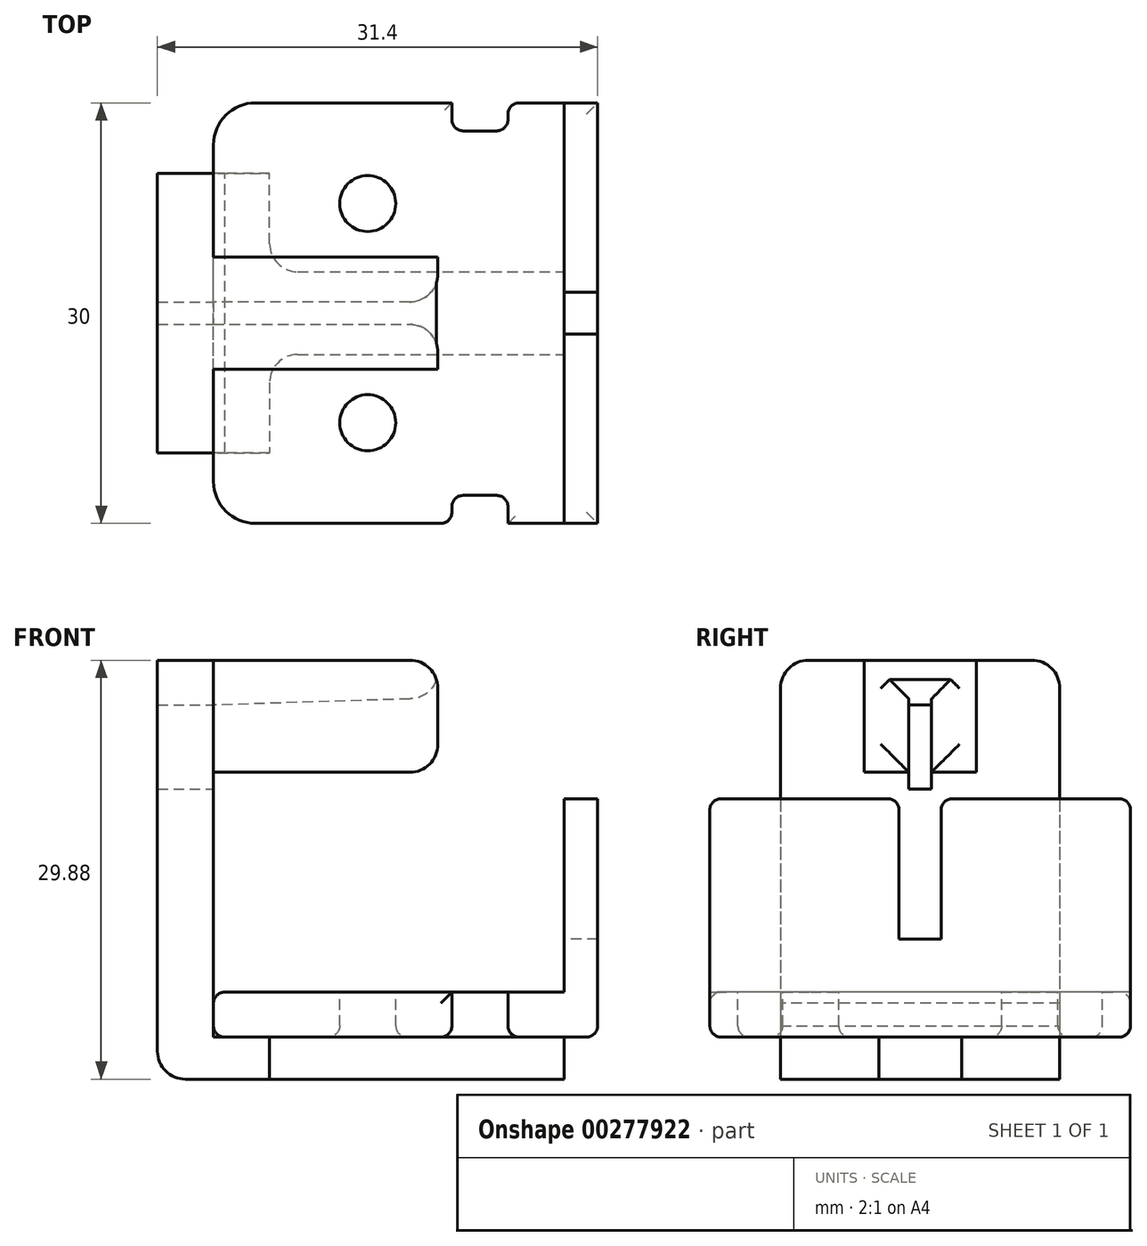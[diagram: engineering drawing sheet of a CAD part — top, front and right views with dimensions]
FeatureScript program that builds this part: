
annotation { "Feature Type Name" : "Feature", "Feature Type Description" : "" }
export const myFeature = defineFeature(function(context is Context, id is Id, definition is map)
    precondition{}
    {
        {
            var Q0;
            Q0=qCreatedBy(makeId("Right.planeOp"),FACE);
            var sketch = newSketch(context, id + "F0", { "sketchPlane" : qUnion([Q0])});
            skPoint(sketch, "E0.middle", {"position": v(0, 9.52) * mm});
            skLineSegment(sketch, "E1.bottom", {"start": v(-15, -0.58) * mm, "end": v(15, -0.58) * mm});
            skLineSegment(sketch, "E2.top", {"start": v(1.5, 6.42) * mm, "end": v(-1.5, 6.42) * mm});
            skLineSegment(sketch, "E2.left", {"start": v(1.5, 14.42) * mm, "end": v(1.5, 6.42) * mm});
            skLineSegment(sketch, "E2.right", {"start": v(-1.5, 14.42) * mm, "end": v(-1.5, 6.42) * mm});
            skPoint(sketch, "E2.middle", {"position": v(0, 10.42) * mm});
            skLineSegment(sketch, "E3", {"start": v(-15, 16.42) * mm, "end": v(-1.5, 16.42) * mm});
            skLineSegment(sketch, "E4", {"start": v(-1.5, 16.42) * mm, "end": v(-1.5, 14.42) * mm});
            skLineSegment(sketch, "E5", {"start": v(1.5, 14.42) * mm, "end": v(1.5, 16.42) * mm});
            skLineSegment(sketch, "E6", {"start": v(1.5, 16.42) * mm, "end": v(15, 16.42) * mm});
            skLineSegment(sketch, "E7", {"start": v(15, 16.42) * mm, "end": v(15, -0.58) * mm});
            skLineSegment(sketch, "E8", {"start": v(-15, -0.58) * mm, "end": v(-15, 16.42) * mm});
            skSolve(sketch);
        }
        {
            var Q0;
            Q0 = qSketchRegion(id + "F0", true);
            extrude(context, id + "F1", {"entities" : qUnion([Q0]), "depth" : 2.4 * mm});
        }
        {
            var Q0;
            Q0=makeQuery(id+"F1.opExtrude","CAP_FACE",FACE,{"disambiguationData":[OSD([sQuery(id+"F0.wireOp",EDGE,"E0.left"),sQuery(id+"F0.wireOp",EDGE,"E0.right"),sQuery(id+"F0.wireOp",EDGE,"E1.bottom"),sQuery(id+"F0.wireOp",EDGE,"E1.left"),sQuery(id+"F0.wireOp",EDGE,"E1.right"),sQuery(id+"F0.wireOp",EDGE,"E2.top"),sQuery(id+"F0.wireOp",EDGE,"E2.left"),sQuery(id+"F0.wireOp",EDGE,"E2.right"),sQuery(id+"F0.wireOp",EDGE,"E3"),sQuery(id+"F0.wireOp",EDGE,"E4"),sQuery(id+"F0.wireOp",EDGE,"E5"),sQuery(id+"F0.wireOp",EDGE,"E6")])],"isStart":true});
            var sketch = newSketch(context, id + "F2", { "sketchPlane" : qUnion([Q0])});
            skLineSegment(sketch, "E9.bottom", {"start": v(-15, -0.58) * mm, "end": v(15, -0.58) * mm});
            skLineSegment(sketch, "E9.top", {"start": v(-15, 2.62) * mm, "end": v(15, 2.62) * mm});
            skLineSegment(sketch, "E9.left", {"start": v(-15, -0.58) * mm, "end": v(-15, 2.62) * mm});
            skLineSegment(sketch, "E9.right", {"start": v(15, -0.58) * mm, "end": v(15, 2.62) * mm});
            skSolve(sketch);
        }
        {
            var Q0;
            Q0 = qSketchRegion(id + "F2", true);
            extrude(context, id + "F3", {"entities" : qUnion([Q0]), "operationType" : NewBodyOperationType.ADD, "depth" : 25 * mm});
        }
        {
            var Q0;
            Q0=makeQuery(id+"F3.opExtrude","SWEPT_FACE",FACE,{"disambiguationData":[OSD([sQuery(id+"F2.wireOp",EDGE,"E9.top")])]});
            var sketch = newSketch(context, id + "F4", { "sketchPlane" : qUnion([Q0])});
            skCircle(sketch, "E10", {"center": v(-14, -7.82) * mm, "radius": 2 * mm});
            skCircle(sketch, "E11.MirrorC", {"center": v(-14, 7.82) * mm, "radius": 2 * mm});
            skCircle(sketch, "E12", {"center": v(-14, 7.82) * mm, "radius": 6 * mm, "construction": true});
            skLineSegment(sketch, "E13", {"start": v(10.5, 1.5) * mm, "end": v(-34.24, 1.5) * mm, "construction": true});
            skLineSegment(sketch, "E14", {"start": v(-34.91, -1.5) * mm, "end": v(11.26, -1.5) * mm, "construction": true});
            skCircle(sketch, "E15.MirrorC", {"center": v(-14, -7.82) * mm, "radius": 6 * mm, "construction": true});
            skSolve(sketch);
        }
        {
            var Q0;
            Q0 = qSketchRegion(id + "F4", true);
            var Q1;
            Q1=makeQuery(id+"F3.boolean.opBoolean","MERGE",FACE,{"derivedFrom":[makeQuery(id+"F1.opExtrude","SWEPT_FACE",FACE,{"disambiguationData":[OSD([sQuery(id+"F0.wireOp",EDGE,"E1.bottom")])]}),makeQuery(id+"F3.opExtrude","SWEPT_FACE",FACE,{"disambiguationData":[OSD([sQuery(id+"F2.wireOp",EDGE,"1xGYJ25z-1f1L-zVY3-qiX9-Y2JeaQydqzHR.bottom")])]})]});
            extrude(context, id + "F5", {"entities" : qUnion([Q0]), "operationType" : NewBodyOperationType.REMOVE, "endBound" : BoundingType.UP_TO_SURFACE, "oppositeDirection" : true, "endBoundEntityFace" : qUnion([Q1]), "depth" : 25 * mm});
        }
        {
            var Q0;
            Q0=makeQuery(id+"F4.imprint","IMPRINT",FACE,{"disambiguationData":[TD([[makeQuery(id+"F4.imprint","IMPRINT",EDGE,{"derivedFrom":sQuery(id+"F4.wireOp",EDGE,"E10")}),-1.0]])]});
            var sketch = newSketch(context, id + "F6", { "sketchPlane" : qUnion([Q0])});
            skLineSegment(sketch, "E16.bottom", {"start": v(-8, 15) * mm, "end": v(-4, 15) * mm});
            skLineSegment(sketch, "E16.top", {"start": v(-8, 13) * mm, "end": v(-4, 13) * mm});
            skLineSegment(sketch, "E16.left", {"start": v(-8, 15) * mm, "end": v(-8, 13) * mm});
            skLineSegment(sketch, "E16.right", {"start": v(-4, 15) * mm, "end": v(-4, 13) * mm});
            skLineSegment(sketch, "E17.MirrorCS", {"start": v(-8, -13) * mm, "end": v(-4, -13) * mm});
            skLineSegment(sketch, "E18.MirrorCS", {"start": v(-4, -15) * mm, "end": v(-4, -13) * mm});
            skLineSegment(sketch, "E19.MirrorCS", {"start": v(-8, -15) * mm, "end": v(-4, -15) * mm});
            skLineSegment(sketch, "E20.MirrorCS", {"start": v(-8, -15) * mm, "end": v(-8, -13) * mm});
            skSolve(sketch);
        }
        {
            var Q0;
            Q0 = qSketchRegion(id + "F6", true);
            var Q1;
            Q1=makeQuery(id+"F3.boolean.opBoolean","MERGE",FACE,{"derivedFrom":[makeQuery(id+"F1.opExtrude","SWEPT_FACE",FACE,{"disambiguationData":[OSD([sQuery(id+"F0.wireOp",EDGE,"E1.bottom")])]}),makeQuery(id+"F3.opExtrude","SWEPT_FACE",FACE,{"disambiguationData":[OSD([sQuery(id+"F2.wireOp",EDGE,"E9.bottom")])]})]});
            extrude(context, id + "F7", {"entities" : qUnion([Q0]), "operationType" : NewBodyOperationType.REMOVE, "endBound" : BoundingType.UP_TO_SURFACE, "oppositeDirection" : true, "endBoundEntityFace" : qUnion([Q1]), "depth" : 25 * mm});
        }
        {
            var Q0;
            Q0=makeQuery(id+"F3.boolean.opBoolean","MERGE",FACE,{"derivedFrom":[makeQuery(id+"F1.opExtrude","SWEPT_FACE",FACE,{"disambiguationData":[OSD([sQuery(id+"F0.wireOp",EDGE,"E1.bottom")])]}),makeQuery(id+"F3.opExtrude","SWEPT_FACE",FACE,{"disambiguationData":[OSD([sQuery(id+"F2.wireOp",EDGE,"1xGYJ25z-1f1L-zVY3-qiX9-Y2JeaQydqzHR.bottom")])]})]});
            var Q1;
            Q1=makeQuery(id+"F1.opExtrude","SWEPT_EDGE",EDGE,{"disambiguationData":[OSD([sQuery(id+"F0.wireOp",EDGE,"E0.left"),sQuery(id+"F0.wireOp",EDGE,"E6")])]});
            var Q2;
            Q2=makeQuery(id+"F1.opExtrude","SWEPT_EDGE",EDGE,{"disambiguationData":[OSD([sQuery(id+"F0.wireOp",EDGE,"E5"),sQuery(id+"F0.wireOp",EDGE,"E6")])]});
            var Q3;
            Q3=makeQuery(id+"F1.opExtrude","SWEPT_EDGE",EDGE,{"disambiguationData":[OSD([sQuery(id+"F0.wireOp",EDGE,"E3"),sQuery(id+"F0.wireOp",EDGE,"E4")])]});
            var Q4;
            Q4=makeQuery(id+"F1.opExtrude","SWEPT_EDGE",EDGE,{"disambiguationData":[OSD([sQuery(id+"F0.wireOp",EDGE,"E0.right"),sQuery(id+"F0.wireOp",EDGE,"E3")])]});
            var Q5;
            Q5=makeQuery(id+"F7.boolean.opBoolean","COPY",EDGE,{"derivedFrom":makeQuery(id+"F7.opExtrude","SWEPT_EDGE",EDGE,{"disambiguationData":[OSD([sQuery(id+"F0.wireOp",EDGE,"E7"),sQuery(id+"F2.wireOp",EDGE,"E9.top"),sQuery(id+"F2.wireOp",EDGE,"E9.left"),sQuery(id+"F6.wireOp",EDGE,"E16.bottom"),sQuery(id+"F6.wireOp",EDGE,"E16.left")])]})});
            var Q6;
            Q6=makeQuery(id+"F7.boolean.opBoolean","COPY",EDGE,{"derivedFrom":makeQuery(id+"F7.opExtrude","SWEPT_EDGE",EDGE,{"disambiguationData":[OSD([sQuery(id+"F0.wireOp",EDGE,"E7"),sQuery(id+"F2.wireOp",EDGE,"E9.top"),sQuery(id+"F2.wireOp",EDGE,"E9.left"),sQuery(id+"F6.wireOp",EDGE,"E16.bottom"),sQuery(id+"F6.wireOp",EDGE,"E16.right")])]})});
            var Q7;
            Q7=makeQuery(id+"F7.boolean.opBoolean","COPY",EDGE,{"derivedFrom":makeQuery(id+"F7.opExtrude","SWEPT_EDGE",EDGE,{"disambiguationData":[OSD([sQuery(id+"F0.wireOp",EDGE,"E8"),sQuery(id+"F2.wireOp",EDGE,"E9.top"),sQuery(id+"F2.wireOp",EDGE,"E9.right"),sQuery(id+"F6.wireOp",EDGE,"E18.MirrorCS"),sQuery(id+"F6.wireOp",EDGE,"E19.MirrorCS")])]})});
            var Q8;
            Q8=makeQuery(id+"F7.boolean.opBoolean","COPY",EDGE,{"derivedFrom":makeQuery(id+"F7.opExtrude","SWEPT_EDGE",EDGE,{"disambiguationData":[OSD([sQuery(id+"F0.wireOp",EDGE,"E8"),sQuery(id+"F2.wireOp",EDGE,"E9.top"),sQuery(id+"F2.wireOp",EDGE,"E9.right"),sQuery(id+"F6.wireOp",EDGE,"E19.MirrorCS"),sQuery(id+"F6.wireOp",EDGE,"E20.MirrorCS")])]})});
            var Q9;
            Q9=makeQuery(id+"F7.boolean.opBoolean","COPY",EDGE,{"derivedFrom":makeQuery(id+"F7.opExtrude","SWEPT_EDGE",EDGE,{"disambiguationData":[OSD([sQuery(id+"F6.wireOp",EDGE,"E17.MirrorCS"),sQuery(id+"F6.wireOp",EDGE,"E18.MirrorCS")])]})});
            var Q10;
            Q10=makeQuery(id+"F7.boolean.opBoolean","COPY",EDGE,{"derivedFrom":makeQuery(id+"F7.opExtrude","SWEPT_EDGE",EDGE,{"disambiguationData":[OSD([sQuery(id+"F6.wireOp",EDGE,"E17.MirrorCS"),sQuery(id+"F6.wireOp",EDGE,"E20.MirrorCS")])]})});
            var Q11;
            Q11=makeQuery(id+"F7.boolean.opBoolean","COPY",EDGE,{"derivedFrom":makeQuery(id+"F7.opExtrude","SWEPT_EDGE",EDGE,{"disambiguationData":[OSD([sQuery(id+"F6.wireOp",EDGE,"E16.top"),sQuery(id+"F6.wireOp",EDGE,"E16.left")])]})});
            var Q12;
            Q12=makeQuery(id+"F7.boolean.opBoolean","COPY",EDGE,{"derivedFrom":makeQuery(id+"F7.opExtrude","SWEPT_EDGE",EDGE,{"disambiguationData":[OSD([sQuery(id+"F6.wireOp",EDGE,"E16.top"),sQuery(id+"F6.wireOp",EDGE,"E16.right")])]})});
            var Q13;
            Q13=makeQuery(id+"F7.boolean.opBoolean","COPY",EDGE,{"derivedFrom":makeQuery(id+"F7.opExtrude","CAP_EDGE",EDGE,{"disambiguationData":[OSD([sQuery(id+"F6.wireOp",EDGE,"E16.top")])],"isStart":true})});
            var Q14;
            Q14=makeQuery(id+"F7.boolean.opBoolean","COPY",EDGE,{"derivedFrom":makeQuery(id+"F7.opExtrude","CAP_EDGE",EDGE,{"disambiguationData":[OSD([sQuery(id+"F6.wireOp",EDGE,"E17.MirrorCS")])],"isStart":true})});
            var Q15;
            {var subQ0=sQuery(id+"F2.wireOp",EDGE,"E9.left");var subQ1=sQuery(id+"F2.wireOp",EDGE,"E9.top");var subQ2=sQuery(id+"F0.wireOp",EDGE,"E7");Q15=makeQuery(id+"F7.boolean.opBoolean","SPLIT",EDGE,{"disambiguationData":[TD([makeQuery(id+"F7.opExtrude","SWEPT_FACE",FACE,{"disambiguationData":[OSD([sQuery(id+"F6.wireOp",EDGE,"E16.left")])]})])],"derivedFrom":makeQuery(id+"F3.opExtrude","SWEPT_EDGE",EDGE,{"disambiguationData":[OSD([subQ2,subQ1,subQ0])]})});}
            var Q16;
            {var subQ0=sQuery(id+"F2.wireOp",EDGE,"E9.right");var subQ1=sQuery(id+"F2.wireOp",EDGE,"E9.top");var subQ2=sQuery(id+"F0.wireOp",EDGE,"E8");Q16=makeQuery(id+"F7.boolean.opBoolean","SPLIT",EDGE,{"disambiguationData":[TD([makeQuery(id+"F7.opExtrude","SWEPT_FACE",FACE,{"disambiguationData":[OSD([sQuery(id+"F6.wireOp",EDGE,"E20.MirrorCS")])]})])],"derivedFrom":makeQuery(id+"F3.opExtrude","SWEPT_EDGE",EDGE,{"disambiguationData":[OSD([subQ2,subQ1,subQ0])]})});}
            var Q17;
            Q17=makeQuery(id+"F3.opExtrude","CAP_EDGE",EDGE,{"disambiguationData":[OSD([sQuery(id+"F2.wireOp",EDGE,"E9.top")])],"isStart":false});
            fillet(context, id + "F8", {"entities" : qUnion([Q0, Q1, Q2, Q3, Q4, Q5, Q6, Q7, Q8, Q9, Q10, Q11, Q12, Q13, Q14, Q15, Q16, Q17]), "radius" : .8 * mm, "tangentPropagation" : true, "allowEdgeOverflow" : false});
        }
        {
            var Q0;
            Q0=makeQuery(id+"F3.opExtrude","CAP_EDGE",EDGE,{"disambiguationData":[OSD([sQuery(id+"F2.wireOp",EDGE,"E9.left")])],"isStart":false});
            var Q1;
            Q1=makeQuery(id+"F3.opExtrude","CAP_EDGE",EDGE,{"disambiguationData":[OSD([sQuery(id+"F2.wireOp",EDGE,"E9.right")])],"isStart":false});
            var Q2;
            Q2=makeQuery(id+"F3.opExtrude","CAP_EDGE",EDGE,{"disambiguationData":[OSD([sQuery(id+"F2.wireOp",EDGE,"E9.top")])],"isStart":true});
            fillet(context, id + "F9", {"entities" : qUnion([Q0, Q1, Q2]), "radius" : 3 * mm, "tangentPropagation" : true, "allowEdgeOverflow" : false});
        }
        {
            var Q0;
            Q0=makeQuery(id+"F1.opExtrude","CAP_FACE",FACE,{"disambiguationData":[OSD([sQuery(id+"F0.wireOp",EDGE,"E1.bottom"),sQuery(id+"F0.wireOp",EDGE,"E2.top"),sQuery(id+"F0.wireOp",EDGE,"E2.left"),sQuery(id+"F0.wireOp",EDGE,"E2.right"),sQuery(id+"F0.wireOp",EDGE,"E3"),sQuery(id+"F0.wireOp",EDGE,"E4"),sQuery(id+"F0.wireOp",EDGE,"E5"),sQuery(id+"F0.wireOp",EDGE,"E6"),sQuery(id+"F0.wireOp",EDGE,"E7"),sQuery(id+"F0.wireOp",EDGE,"E8")])],"isStart":true});
            cPlane(context, id + "F10", {"entities" : qUnion([Q0]), "cplaneType" : CPlaneType.OFFSET, "offset" : 25 * mm, "width" : 150 * mm, "height" : 150 * mm});
        }
        {
            var Q0;
            Q0=qCreatedBy(id+"F10.planeOp",FACE);
            var sketch = newSketch(context, id + "F11", { "sketchPlane" : qUnion([Q0])});
            skLineSegment(sketch, "E21.bottom", {"start": v(-0.8, 17.1) * mm, "end": v(0.8, 17.1) * mm});
            skLineSegment(sketch, "E21.top", {"start": v(-0.8, 23.1) * mm, "end": v(0.8, 23.1) * mm});
            skLineSegment(sketch, "E21.left", {"start": v(-0.8, 17.1) * mm, "end": v(-0.8, 23.1) * mm});
            skLineSegment(sketch, "E21.right", {"start": v(0.8, 17.1) * mm, "end": v(0.8, 23.1) * mm});
            skPoint(sketch, "E21.middle", {"position": v(0, 20.1) * mm});
            skLineSegment(sketch, "E22.bottom", {"start": v(-9.96, 26.3) * mm, "end": v(9.96, 26.3) * mm});
            skLineSegment(sketch, "E22.top", {"start": v(-9.96, -3.58) * mm, "end": v(9.96, -3.58) * mm});
            skLineSegment(sketch, "E22.left", {"start": v(-9.96, 26.3) * mm, "end": v(-9.96, -3.58) * mm});
            skLineSegment(sketch, "E22.right", {"start": v(9.96, 26.3) * mm, "end": v(9.96, -3.58) * mm});
            skPoint(sketch, "E22.middle", {"position": v(0, 11.36) * mm});
            skSolve(sketch);
        }
        {
            var Q0;
            Q0 = qSketchRegion(id + "F11", true);
            extrude(context, id + "F12", {"entities" : qUnion([Q0]), "depth" : 4 * mm});
        }
        {
            var Q0;
            Q0=makeQuery(id+"F12.opExtrude","CAP_FACE",FACE,{"disambiguationData":[OSD([sQuery(id+"F11.wireOp",EDGE,"E21.bottom"),sQuery(id+"F11.wireOp",EDGE,"E21.top"),sQuery(id+"F11.wireOp",EDGE,"E21.left"),sQuery(id+"F11.wireOp",EDGE,"E21.right"),sQuery(id+"F11.wireOp",EDGE,"E22.bottom"),sQuery(id+"F11.wireOp",EDGE,"E22.top"),sQuery(id+"F11.wireOp",EDGE,"E22.left"),sQuery(id+"F11.wireOp",EDGE,"E22.right")])],"isStart":true});
            var sketch = newSketch(context, id + "F13", { "sketchPlane" : qUnion([Q0])});
            skLineSegment(sketch, "E23.bottom", {"start": v(-4, 18.3) * mm, "end": v(-0.8, 18.3) * mm});
            skLineSegment(sketch, "E23.top", {"start": v(-4, 26.3) * mm, "end": v(4, 26.3) * mm});
            skLineSegment(sketch, "E23.left", {"start": v(-4, 18.3) * mm, "end": v(-4, 26.3) * mm});
            skLineSegment(sketch, "E23.right", {"start": v(4, 18.3) * mm, "end": v(4, 26.3) * mm});
            skPoint(sketch, "E23.middle", {"position": v(0, 22.3) * mm});
            skLineSegment(sketch, "E24.top", {"start": v(-0.8, 23.1) * mm, "end": v(0.8, 23.1) * mm});
            skLineSegment(sketch, "E24.left", {"start": v(-0.8, 18.3) * mm, "end": v(-0.8, 23.1) * mm});
            skLineSegment(sketch, "E24.right", {"start": v(0.8, 18.3) * mm, "end": v(0.8, 23.1) * mm});
            skPoint(sketch, "E24.middle", {"position": v(0, 20.7) * mm});
            skLineSegment(sketch, "E25.trimOffspring", {"start": v(0.8, 18.3) * mm, "end": v(4, 18.3) * mm});
            skSolve(sketch);
        }
        {
            var Q0;
            Q0 = qSketchRegion(id + "F13", true);
            extrude(context, id + "F14", {"entities" : qUnion([Q0]), "operationType" : NewBodyOperationType.ADD, "depth" : 16 * mm});
        }
        {
            var Q0;
            Q0=makeQuery(id+"F14.opExtrude","CAP_EDGE",EDGE,{"disambiguationData":[OSD([sQuery(id+"F13.wireOp",EDGE,"E24.top")])],"isStart":false});
            chamfer(context, id + "F15", {"entities" : qUnion([Q0]), "chamferType" : ChamferType.TWO_OFFSETS, "width1" : 16 * mm, "oppositeDirection" : false, "width2" : .5 * mm, "tangentPropagation" : true});
        }
        {
            var Q0;
            Q0=makeQuery(id+"F12.opExtrude","CAP_FACE",FACE,{"disambiguationData":[OSD([sQuery(id+"F11.wireOp",EDGE,"E21.bottom"),sQuery(id+"F11.wireOp",EDGE,"E21.top"),sQuery(id+"F11.wireOp",EDGE,"E21.left"),sQuery(id+"F11.wireOp",EDGE,"E21.right"),sQuery(id+"F11.wireOp",EDGE,"E22.bottom"),sQuery(id+"F11.wireOp",EDGE,"E22.top"),sQuery(id+"F11.wireOp",EDGE,"E22.left"),sQuery(id+"F11.wireOp",EDGE,"E22.right")])],"isStart":true});
            var sketch = newSketch(context, id + "F16", { "sketchPlane" : qUnion([Q0])});
            skLineSegment(sketch, "E26.bottom", {"start": v(9.96, -3.58) * mm, "end": v(-9.96, -3.58) * mm});
            skLineSegment(sketch, "E26.top", {"start": v(9.96, -0.58) * mm, "end": v(-9.96, -0.58) * mm});
            skLineSegment(sketch, "E26.left", {"start": v(9.96, -3.58) * mm, "end": v(9.96, -0.58) * mm});
            skLineSegment(sketch, "E26.right", {"start": v(-9.96, -3.58) * mm, "end": v(-9.96, -0.58) * mm});
            skSolve(sketch);
        }
        {
            var Q0;
            Q0 = qSketchRegion(id + "F16", true);
            extrude(context, id + "F17", {"entities" : qUnion([Q0]), "operationType" : NewBodyOperationType.ADD, "depth" : 25 * mm});
        }
        {
            var Q0;
            Q0=makeQuery(id+"F3.boolean.opBoolean","MERGE",FACE,{"derivedFrom":[makeQuery(id+"F1.opExtrude","SWEPT_FACE",FACE,{"disambiguationData":[OSD([sQuery(id+"F0.wireOp",EDGE,"E1.bottom")])]}),makeQuery(id+"F3.opExtrude","SWEPT_FACE",FACE,{"disambiguationData":[OSD([sQuery(id+"F2.wireOp",EDGE,"E9.bottom")])]})]});
            var sketch = newSketch(context, id + "F18", { "sketchPlane" : qUnion([Q0])});
            skLineSegment(sketch, "E27.bottom", {"start": v(0, -9.96) * mm, "end": v(-21, -9.96) * mm});
            skLineSegment(sketch, "E27.top", {"start": v(0, -2.96) * mm, "end": v(-21, -2.96) * mm});
            skLineSegment(sketch, "E27.left", {"start": v(0, -9.96) * mm, "end": v(0, -2.96) * mm});
            skLineSegment(sketch, "E27.right", {"start": v(-21, -9.96) * mm, "end": v(-21, -2.96) * mm});
            skLineSegment(sketch, "E28.MirrorCS", {"start": v(0, 2.96) * mm, "end": v(-21, 2.96) * mm});
            skLineSegment(sketch, "E29.MirrorCS", {"start": v(-21, 9.96) * mm, "end": v(-21, 2.96) * mm});
            skLineSegment(sketch, "E30.MirrorCS", {"start": v(0, 9.96) * mm, "end": v(-21, 9.96) * mm});
            skLineSegment(sketch, "E31.MirrorCS", {"start": v(0, 9.96) * mm, "end": v(0, 2.96) * mm});
            skSolve(sketch);
        }
        {
            var Q0;
            Q0 = qSketchRegion(id + "F18", true);
            var Q1;
            Q1=makeQuery(id+"F17.boolean.opBoolean","MERGE",FACE,{"derivedFrom":[makeQuery(id+"F12.opExtrude","SWEPT_FACE",FACE,{"disambiguationData":[OSD([sQuery(id+"F11.wireOp",EDGE,"E22.top")])]}),makeQuery(id+"F17.opExtrude","SWEPT_FACE",FACE,{"disambiguationData":[OSD([sQuery(id+"F16.wireOp",EDGE,"E26.bottom")])]})]});
            extrude(context, id + "F19", {"entities" : qUnion([Q0]), "operationType" : NewBodyOperationType.REMOVE, "endBound" : BoundingType.UP_TO_SURFACE, "endBoundEntityFace" : qUnion([Q1]), "depth" : 25 * mm});
        }
        {
            var Q0;
            Q0=makeQuery(id+"F19.boolean.opBoolean","COPY",EDGE,{"derivedFrom":makeQuery(id+"F19.opExtrude","SWEPT_EDGE",EDGE,{"disambiguationData":[OSD([sQuery(id+"F18.wireOp",EDGE,"E27.top"),sQuery(id+"F18.wireOp",EDGE,"E27.left")])]})});
            var Q1;
            Q1=makeQuery(id+"F19.boolean.opBoolean","COPY",EDGE,{"derivedFrom":makeQuery(id+"F19.opExtrude","SWEPT_EDGE",EDGE,{"disambiguationData":[OSD([sQuery(id+"F18.wireOp",EDGE,"E28.MirrorCS"),sQuery(id+"F18.wireOp",EDGE,"E31.MirrorCS")])]})});
            var Q2;
            Q2=makeQuery(id+"F19.boolean.opBoolean","COPY",EDGE,{"derivedFrom":makeQuery(id+"F19.opExtrude","SWEPT_EDGE",EDGE,{"disambiguationData":[OSD([sQuery(id+"F18.wireOp",EDGE,"E27.top"),sQuery(id+"F18.wireOp",EDGE,"E27.right")])]})});
            var Q3;
            Q3=makeQuery(id+"F19.boolean.opBoolean","COPY",EDGE,{"derivedFrom":makeQuery(id+"F19.opExtrude","SWEPT_EDGE",EDGE,{"disambiguationData":[OSD([sQuery(id+"F18.wireOp",EDGE,"E28.MirrorCS"),sQuery(id+"F18.wireOp",EDGE,"E29.MirrorCS")])]})});
            var Q4;
            Q4=makeQuery(id+"F19.boolean.opBoolean","COPY",EDGE,{"derivedFrom":makeQuery(id+"F19.opExtrude","SWEPT_EDGE",EDGE,{"disambiguationData":[OSD([sQuery(id+"F18.wireOp",EDGE,"E29.MirrorCS"),sQuery(id+"F18.wireOp",EDGE,"E30.MirrorCS")])]})});
            var Q5;
            Q5=makeQuery(id+"F19.boolean.opBoolean","COPY",EDGE,{"derivedFrom":makeQuery(id+"F19.opExtrude","SWEPT_EDGE",EDGE,{"disambiguationData":[OSD([sQuery(id+"F18.wireOp",EDGE,"E27.bottom"),sQuery(id+"F18.wireOp",EDGE,"E27.right")])]})});
            var Q6;
            Q6=makeQuery(id+"F12.opExtrude","CAP_EDGE",EDGE,{"disambiguationData":[OSD([sQuery(id+"F11.wireOp",EDGE,"E22.top")])],"isStart":false});
            var Q7;
            Q7=makeQuery(id+"F14.opExtrude","CAP_EDGE",EDGE,{"disambiguationData":[OSD([sQuery(id+"F13.wireOp",EDGE,"E23.bottom")])],"isStart":false});
            var Q8;
            Q8=makeQuery(id+"F14.opExtrude","CAP_EDGE",EDGE,{"disambiguationData":[OSD([sQuery(id+"F13.wireOp",EDGE,"E25.trimOffspring")])],"isStart":false});
            var Q9;
            Q9=makeQuery(id+"F14.opExtrude","CAP_EDGE",EDGE,{"disambiguationData":[OSD([sQuery(id+"F13.wireOp",EDGE,"E23.top")])],"isStart":false});
            var Q10;
            Q10=makeQuery(id+"F14.opExtrude","CAP_EDGE",EDGE,{"disambiguationData":[OSD([sQuery(id+"F13.wireOp",EDGE,"E23.right")])],"isStart":true});
            var Q11;
            Q11=makeQuery(id+"F14.opExtrude","CAP_EDGE",EDGE,{"disambiguationData":[OSD([sQuery(id+"F13.wireOp",EDGE,"E23.left")])],"isStart":true});
            var Q12;
            Q12=makeQuery(id+"F12.opExtrude","SWEPT_EDGE",EDGE,{"disambiguationData":[OSD([sQuery(id+"F11.wireOp",EDGE,"E22.bottom"),sQuery(id+"F11.wireOp",EDGE,"E22.right")])]});
            var Q13;
            Q13=makeQuery(id+"F12.opExtrude","SWEPT_EDGE",EDGE,{"disambiguationData":[OSD([sQuery(id+"F11.wireOp",EDGE,"E22.bottom"),sQuery(id+"F11.wireOp",EDGE,"E22.left")])]});
            var Q14;
            Q14=makeQuery(id+"F14.opExtrude","CAP_EDGE",EDGE,{"disambiguationData":[OSD([sQuery(id+"F13.wireOp",EDGE,"E24.left")])],"isStart":false});
            var Q15;
            Q15=makeQuery(id+"F14.opExtrude","CAP_EDGE",EDGE,{"disambiguationData":[OSD([sQuery(id+"F13.wireOp",EDGE,"E24.right")])],"isStart":false});
            var Q16;
            {var subQ0=sQuery(id+"F13.wireOp",EDGE,"E24.top");Q16=makeQuery(id+"F15.opChamfer","BLEND_EDGE",EDGE,{"blendedFrom":[makeQuery(id+"F14.opExtrude","CAP_EDGE",EDGE,{"disambiguationData":[OSD([subQ0])],"isStart":false}),makeQuery(id+"F14.opExtrude","CAP_FACE",FACE,{"disambiguationData":[OSD([sQuery(id+"F13.wireOp",EDGE,"E23.bottom"),sQuery(id+"F13.wireOp",EDGE,"E23.top"),sQuery(id+"F13.wireOp",EDGE,"E23.left"),sQuery(id+"F13.wireOp",EDGE,"E23.right"),subQ0,sQuery(id+"F13.wireOp",EDGE,"E24.left"),sQuery(id+"F13.wireOp",EDGE,"E24.right"),sQuery(id+"F13.wireOp",EDGE,"E25.trimOffspring")])],"isStart":false})],"blendedInto":[makeQuery(id+"F14.opExtrude","CAP_FACE",FACE,{"disambiguationData":[OSD([sQuery(id+"F13.wireOp",EDGE,"E23.bottom"),sQuery(id+"F13.wireOp",EDGE,"E23.top"),sQuery(id+"F13.wireOp",EDGE,"E23.left"),sQuery(id+"F13.wireOp",EDGE,"E23.right"),subQ0,sQuery(id+"F13.wireOp",EDGE,"E24.left"),sQuery(id+"F13.wireOp",EDGE,"E24.right"),sQuery(id+"F13.wireOp",EDGE,"E25.trimOffspring")])],"isStart":false})]});}
            fillet(context, id + "F20", {"entities" : qUnion([Q0, Q1, Q2, Q3, Q4, Q5, Q6, Q7, Q8, Q9, Q10, Q11, Q12, Q13, Q14, Q15, Q16]), "radius" : 2 * mm, "tangentPropagation" : true, "allowEdgeOverflow" : false});
        }
    });
